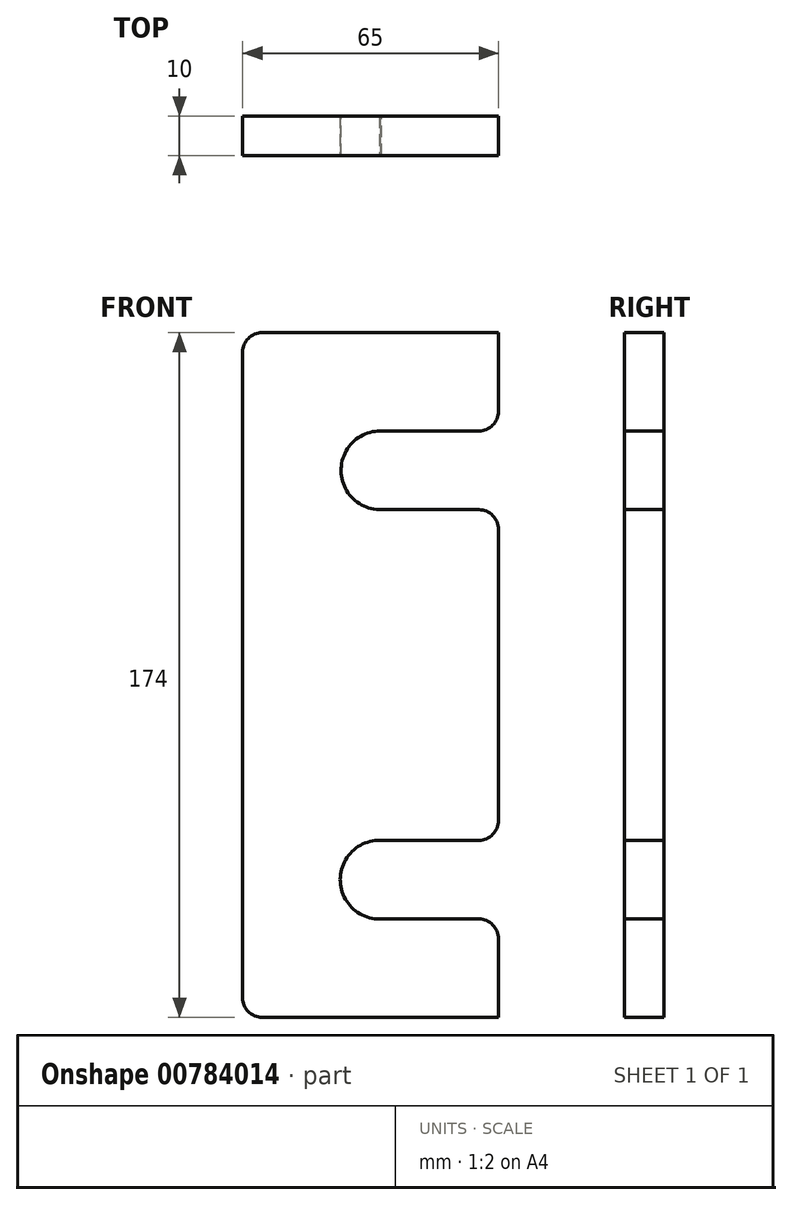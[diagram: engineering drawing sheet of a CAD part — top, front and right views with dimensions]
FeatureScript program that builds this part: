
annotation { "Feature Type Name" : "Feature", "Feature Type Description" : "" }
export const myFeature = defineFeature(function(context is Context, id is Id, definition is map)
    precondition{}
    {
        {
            var Q0;
            Q0=qCreatedBy(makeId("Front.planeOp"),FACE);
            var sketch = newSketch(context, id + "F0", { "sketchPlane" : qUnion([Q0])});
            skLineSegment(sketch, "E0.bottom", {"start": v(-43.3, 115.6) * mm, "end": v(96.7, 115.6) * mm});
            skLineSegment(sketch, "E0.top", {"start": v(-43.3, -58.4) * mm, "end": v(96.7, -58.4) * mm});
            skLineSegment(sketch, "E0.left", {"start": v(-48.3, 110.6) * mm, "end": v(-48.3, -53.4) * mm});
            skLineSegment(sketch, "E0.right", {"start": v(101.7, 110.6) * mm, "end": v(101.7, -53.4) * mm});
            skPoint(sketch, "E1.visualSharp", {"position": v(-48.3, 115.6) * mm});
            skArc(sketch, "E1.filletArc", {"start": v(-43.3, 115.6) * mm, "mid": v(-46.83, 114.13) * mm, "end": v(-48.3, 110.6) * mm});
            skPoint(sketch, "E2.visualSharp", {"position": v(101.7, 115.6) * mm});
            skArc(sketch, "E2.filletArc", {"start": v(101.7, 110.6) * mm, "mid": v(100.25, 114.13) * mm, "end": v(96.7, 115.6) * mm});
            skPoint(sketch, "E3.visualSharp", {"position": v(101.7, -58.4) * mm});
            skArc(sketch, "E3.filletArc", {"start": v(96.7, -58.4) * mm, "mid": v(100.25, -56.94) * mm, "end": v(101.7, -53.4) * mm});
            skPoint(sketch, "E4.visualSharp", {"position": v(-48.3, -58.4) * mm});
            skArc(sketch, "E4.filletArc", {"start": v(-48.3, -53.4) * mm, "mid": v(-46.83, -56.94) * mm, "end": v(-43.3, -58.4) * mm});
            skLineSegment(sketch, "E5", {"start": v(26.7, 115.6) * mm, "end": v(26.7, -58.4) * mm, "construction": true});
            skLineSegment(sketch, "E6", {"start": v(66.7, 115.6) * mm, "end": v(66.7, -58.4) * mm, "construction": true});
            skCircle(sketch, "E7", {"center": v(66.7, 80.6) * mm, "radius": 10 * mm});
            skCircle(sketch, "E8", {"center": v(66.7, -23.4) * mm, "radius": 10 * mm});
            skCircle(sketch, "E9.MirrorC", {"center": v(-13.3, 80.6) * mm, "radius": 10 * mm});
            skCircle(sketch, "E10.MirrorC", {"center": v(-13.3, -23.4) * mm, "radius": 10 * mm});
            skSolve(sketch);
        }
        {
            var Q0;
            Q0 = qSketchRegion(id + "F0", true);
            extrude(context, id + "F1", {"entities" : qUnion([Q0]), "depth" : 10 * mm, "offsetDistance" : 25 * mm});
        }
        {
            var Q0;
            Q0=makeQuery(id+"F1.opExtrude","CAP_FACE",FACE,{"disambiguationData":[OSD([sQuery(id+"F0.wireOp",EDGE,"E0.bottom"),sQuery(id+"F0.wireOp",EDGE,"E0.top"),sQuery(id+"F0.wireOp",EDGE,"E0.left"),sQuery(id+"F0.wireOp",EDGE,"E0.right"),sQuery(id+"F0.wireOp",EDGE,"E1.filletArc"),sQuery(id+"F0.wireOp",EDGE,"E2.filletArc"),sQuery(id+"F0.wireOp",EDGE,"E3.filletArc"),sQuery(id+"F0.wireOp",EDGE,"E4.filletArc"),sQuery(id+"F0.wireOp",EDGE,"E7"),sQuery(id+"F0.wireOp",EDGE,"E8"),sQuery(id+"F0.wireOp",EDGE,"E9.MirrorC"),sQuery(id+"F0.wireOp",EDGE,"E10.MirrorC")])],"isStart":false});
            var sketch = newSketch(context, id + "F2", { "sketchPlane" : qUnion([Q0])});
            skLineSegment(sketch, "E11", {"start": v(16.7, 115.6) * mm, "end": v(16.7, 95.6) * mm});
            skLineSegment(sketch, "E12", {"start": v(-13.61, 70.6) * mm, "end": v(11.7, 70.6) * mm});
            skLineSegment(sketch, "E13", {"start": v(-13.3, 90.6) * mm, "end": v(11.7, 90.6) * mm});
            skLineSegment(sketch, "E14.trimOffspring", {"start": v(16.7, 65.6) * mm, "end": v(16.7, -8.4) * mm});
            skLineSegment(sketch, "E15", {"start": v(-13.34, -13.4) * mm, "end": v(11.7, -13.4) * mm});
            skLineSegment(sketch, "E16", {"start": v(-13.49, -33.4) * mm, "end": v(11.7, -33.4) * mm});
            skLineSegment(sketch, "E17.trimOffspring", {"start": v(16.7, -38.4) * mm, "end": v(16.7, -58.4) * mm});
            skPoint(sketch, "E18.visualSharp", {"position": v(16.7, 70.6) * mm});
            skArc(sketch, "E18.filletArc", {"start": v(16.7, 65.6) * mm, "mid": v(15.25, 69.14) * mm, "end": v(11.7, 70.6) * mm});
            skPoint(sketch, "E19.visualSharp", {"position": v(16.7, 90.6) * mm});
            skArc(sketch, "E19.filletArc", {"start": v(11.7, 90.6) * mm, "mid": v(15.25, 92.06) * mm, "end": v(16.7, 95.6) * mm});
            skPoint(sketch, "E20.visualSharp", {"position": v(16.7, -13.4) * mm});
            skArc(sketch, "E20.filletArc", {"start": v(11.7, -13.4) * mm, "mid": v(15.25, -11.94) * mm, "end": v(16.7, -8.4) * mm});
            skPoint(sketch, "E21.visualSharp", {"position": v(16.7, -33.4) * mm});
            skArc(sketch, "E21.filletArc", {"start": v(16.7, -38.4) * mm, "mid": v(15.25, -34.87) * mm, "end": v(11.7, -33.4) * mm});
            skLineSegment(sketch, "E22", {"start": v(16.7, 115.6) * mm, "end": v(128.53, 115.6) * mm});
            skLineSegment(sketch, "E23", {"start": v(128.53, 115.6) * mm, "end": v(128.53, -58.4) * mm});
            skLineSegment(sketch, "E24", {"start": v(128.53, -58.4) * mm, "end": v(16.7, -58.4) * mm});
            skArc(sketch, "E25", {"start": v(-13.3, 90.6) * mm, "mid": v(-23.29, 80.76) * mm, "end": v(-13.61, 70.6) * mm});
            skArc(sketch, "E26", {"start": v(-13.34, -13.4) * mm, "mid": v(-23.49, -23.33) * mm, "end": v(-13.49, -33.4) * mm});
            skSolve(sketch);
        }
        {
            var Q0;
            Q0 = qSketchRegion(id + "F2", true);
            extrude(context, id + "F3", {"entities" : qUnion([Q0]), "operationType" : NewBodyOperationType.REMOVE, "oppositeDirection" : true, "depth" : 25 * mm, "offsetDistance" : 25 * mm});
        }
    });
